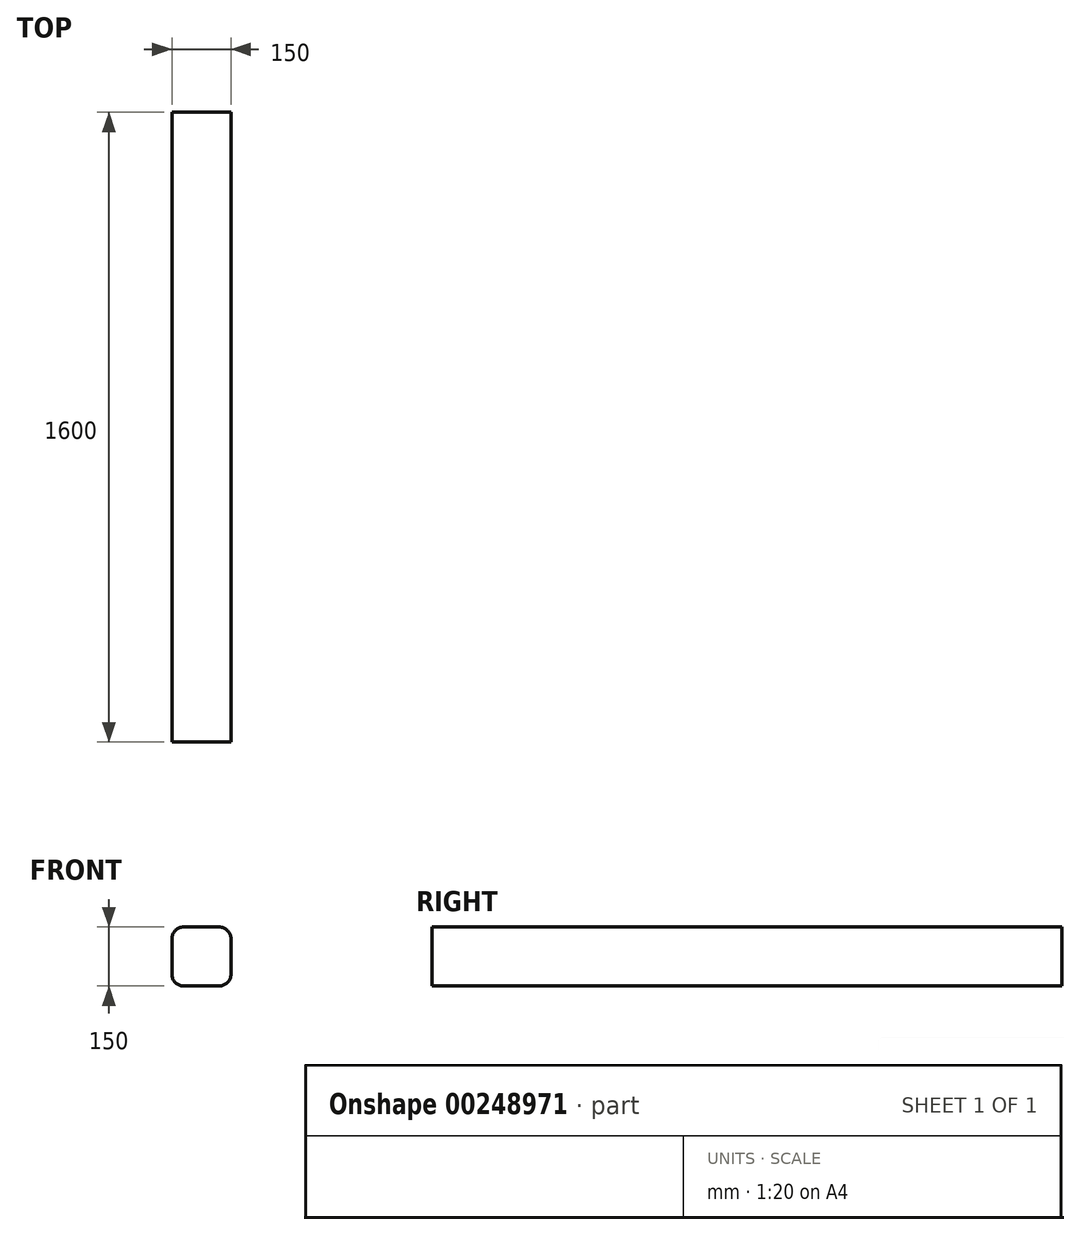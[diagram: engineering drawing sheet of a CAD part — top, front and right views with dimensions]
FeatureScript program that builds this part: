
annotation { "Feature Type Name" : "Feature", "Feature Type Description" : "" }
export const myFeature = defineFeature(function(context is Context, id is Id, definition is map)
    precondition{}
    {
        {
            var Q0;
            Q0=qCreatedBy(makeId("Front.planeOp"),FACE);
            var sketch = newSketch(context, id + "F0", { "sketchPlane" : qUnion([Q0])});
            skLineSegment(sketch, "E0.bottom", {"start": v(45, 75) * mm, "end": v(-45, 75) * mm});
            skLineSegment(sketch, "E0.top", {"start": v(45, -75) * mm, "end": v(-45, -75) * mm});
            skLineSegment(sketch, "E0.left", {"start": v(75, 45) * mm, "end": v(75, -45) * mm});
            skLineSegment(sketch, "E0.right", {"start": v(-75, 45) * mm, "end": v(-75, -45) * mm});
            skPoint(sketch, "E0.middle", {"position": v(0, 0) * mm});
            skPoint(sketch, "E1.visualSharp", {"position": v(-75, 75) * mm});
            skArc(sketch, "E1.filletArc", {"start": v(-45, 75) * mm, "mid": v(-66.21, 66.21) * mm, "end": v(-75, 45) * mm});
            skPoint(sketch, "E2.visualSharp", {"position": v(75, 75) * mm});
            skArc(sketch, "E2.filletArc", {"start": v(75, 45) * mm, "mid": v(66.21, 66.21) * mm, "end": v(45, 75) * mm});
            skPoint(sketch, "E3.visualSharp", {"position": v(75, -75) * mm});
            skArc(sketch, "E3.filletArc", {"start": v(45, -75) * mm, "mid": v(66.21, -66.21) * mm, "end": v(75, -45) * mm});
            skPoint(sketch, "E4.visualSharp", {"position": v(-75, -75) * mm});
            skArc(sketch, "E4.filletArc", {"start": v(-75, -45) * mm, "mid": v(-66.21, -66.21) * mm, "end": v(-45, -75) * mm});
            skSolve(sketch);
        }
        {
            var Q0;
            Q0 = qSketchRegion(id + "F0", true);
            extrude(context, id + "F1", {"entities" : qUnion([Q0]), "depth" : 1600 * mm});
        }
    });
